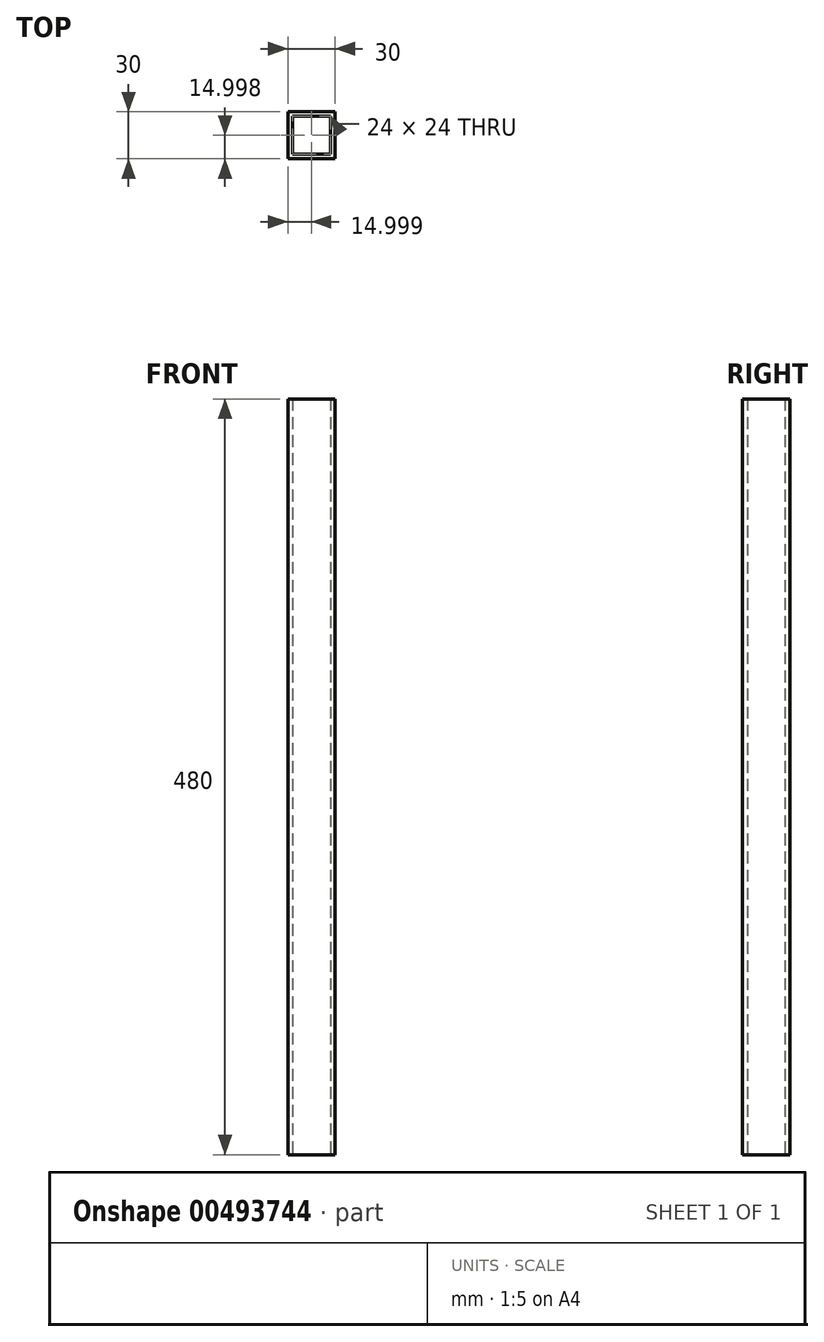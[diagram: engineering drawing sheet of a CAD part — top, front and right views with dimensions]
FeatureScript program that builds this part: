
annotation { "Feature Type Name" : "Feature", "Feature Type Description" : "" }
export const myFeature = defineFeature(function(context is Context, id is Id, definition is map)
    precondition{}
    {
        {
            var Q0;
            Q0=qCreatedBy(makeId("Top.planeOp"),FACE);
            var sketch = newSketch(context, id + "F0", { "sketchPlane" : qUnion([Q0])});
            skLineSegment(sketch, "E0.bottom", {"start": v(-21, 16.5) * mm, "end": v(9, 16.5) * mm});
            skLineSegment(sketch, "E0.top", {"start": v(-21, -13.5) * mm, "end": v(9, -13.5) * mm});
            skLineSegment(sketch, "E0.left", {"start": v(-21, 16.5) * mm, "end": v(-21, -13.5) * mm});
            skLineSegment(sketch, "E0.right", {"start": v(9, 16.5) * mm, "end": v(9, -13.5) * mm});
            skLineSegment(sketch, "E1.bottom", {"start": v(-18, 13.5) * mm, "end": v(6, 13.5) * mm});
            skLineSegment(sketch, "E1.top", {"start": v(-18, -10.5) * mm, "end": v(6, -10.5) * mm});
            skLineSegment(sketch, "E1.left", {"start": v(-18, 13.5) * mm, "end": v(-18, -10.5) * mm});
            skLineSegment(sketch, "E1.right", {"start": v(6, 13.5) * mm, "end": v(6, -10.5) * mm});
            skSolve(sketch);
        }
        {
            var Q0;
            Q0=qSketchRegion(id+"F0",true);
            extrude(context, id + "F1", {"entities" : qUnion([Q0]), "depth" : 480 * mm});
        }
    });
